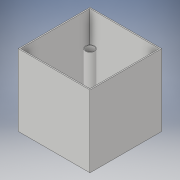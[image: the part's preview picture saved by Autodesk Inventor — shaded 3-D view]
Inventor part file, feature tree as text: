
AUTODESK INVENTOR PART (.ipt)
format: ipt  version: 2019.1 (Build 231200000, 200)  size: 118,784 bytes
history: native  units: mm
features: extrude x3, sketch x3, other x1, projected_geometry x1
ambient origin geometry x8: Origin, YZ Plane, XZ Plane, XY Plane, X Axis, Y Axis, Z Axis, Center Point
bodies: Body1 (feature_tree)
feature tree (8):
  other  "ソリッド1"
  extrude  "押し出し1"  Depth=310.0mm
  extrude  "押し出し2"  Depth=310.0mm
  extrude  "押し出し3"  Depth=10.0mm TaperAngle=0.0deg
  sketch  "スケッチ1"
  sketch  "スケッチ2"
  projected_geometry  "投影ループ1"
  sketch  "スケッチ3"
